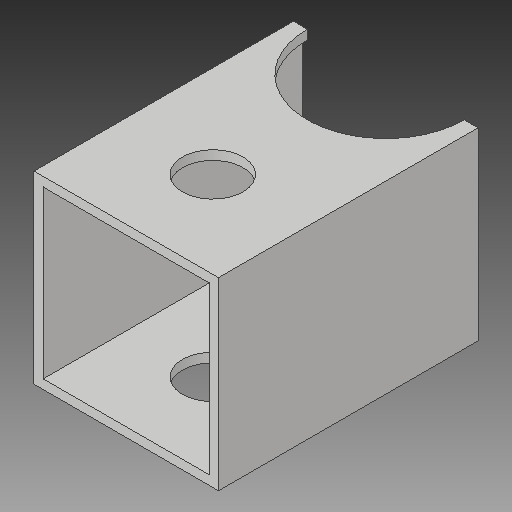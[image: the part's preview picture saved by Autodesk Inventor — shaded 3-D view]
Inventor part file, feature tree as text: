
AUTODESK INVENTOR PART (.ipt)
format: ipt  version: 2018 (Build 220112000, 112)  size: 118,784 bytes
history: native  units: mm
features: sketch x3, extrude x2, other x1, hole x1
ambient origin geometry x8: Origin, YZ Plane, XZ Plane, XY Plane, X Axis, Y Axis, Z Axis, Center Point
bodies: Body1 (feature_tree)
feature tree (7):
  other  "ソリッド1"
  extrude  "押し出し1"  Depth=32.0mm
  extrude  "押し出し2"  Depth=32.0mm
  hole  "穴1"  [1 undecoded]
  sketch  "スケッチ1"
  sketch  "スケッチ2"
  sketch  "スケッチ3"
note: 1 required parameter value undecoded (feature->parameter linkage not recoverable at this tier; creation-order binding heuristic only, values carry confidence <= 0.55)
